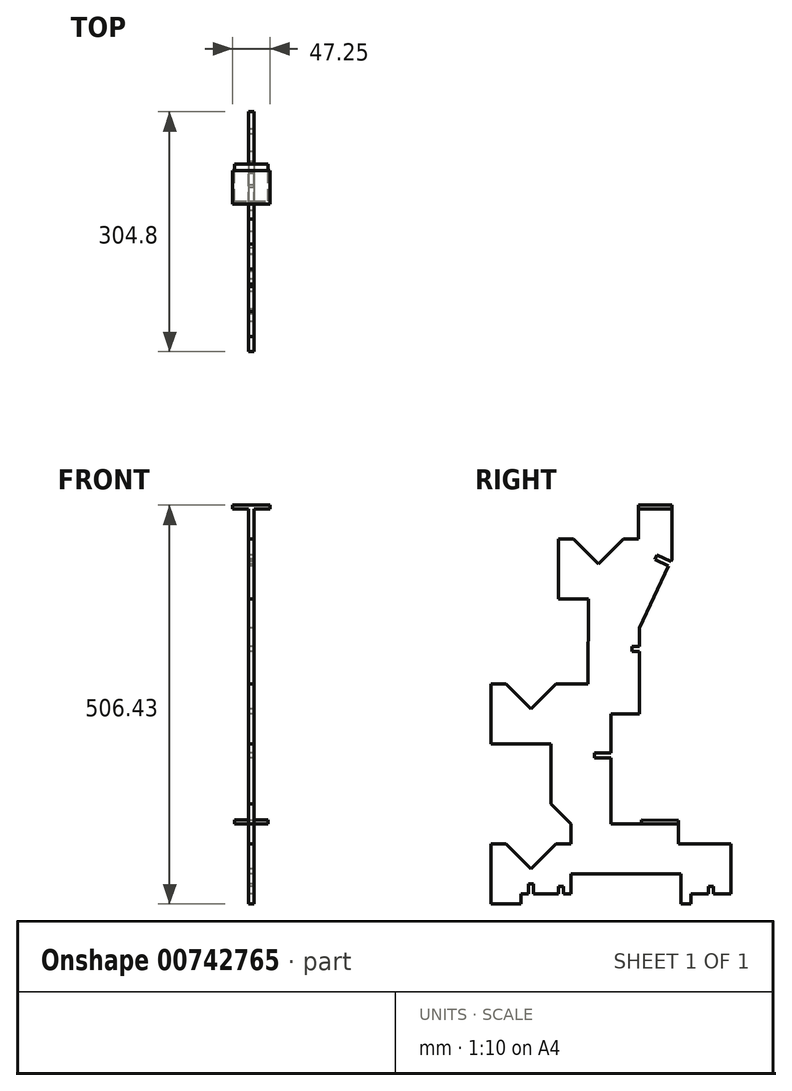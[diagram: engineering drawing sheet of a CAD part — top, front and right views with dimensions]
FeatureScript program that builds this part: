
annotation { "Feature Type Name" : "Feature", "Feature Type Description" : "" }
export const myFeature = defineFeature(function(context is Context, id is Id, definition is map)
    precondition{}
    {
        {
            var Q0;
            Q0=qCreatedBy(makeId("Right.planeOp"),FACE);
            var sketch = newSketch(context, id + "F0", { "sketchPlane" : qUnion([Q0])});
            skLineSegment(sketch, "E0", {"start": v(-497.04, 173.21) * mm, "end": v(-516.09, 173.21) * mm});
            skLineSegment(sketch, "E1", {"start": v(-516.09, 173.21) * mm, "end": v(-516.09, 97.01) * mm});
            skLineSegment(sketch, "E2", {"start": v(-516.09, 97.01) * mm, "end": v(-477.99, 97.01) * mm});
            skLineSegment(sketch, "E3", {"start": v(-477.99, 97.01) * mm, "end": v(-477.99, 109.71) * mm});
            skLineSegment(sketch, "E4", {"start": v(-477.99, 109.71) * mm, "end": v(-468.46, 109.71) * mm});
            skLineSegment(sketch, "E5", {"start": v(-414.49, 109.71) * mm, "end": v(-414.49, 135.11) * mm});
            skLineSegment(sketch, "E6", {"start": v(-433.54, 173.21) * mm, "end": v(-465.29, 141.46) * mm});
            skLineSegment(sketch, "E7", {"start": v(-465.29, 141.46) * mm, "end": v(-497.04, 173.21) * mm});
            skLineSegment(sketch, "E8", {"start": v(-414.49, 135.11) * mm, "end": v(-274.79, 135.11) * mm});
            skLineSegment(sketch, "E9", {"start": v(-277.55, 173.21) * mm, "end": v(-277.55, 198.5) * mm});
            skLineSegment(sketch, "E10", {"start": v(-277.55, 198.5) * mm, "end": v(-363.69, 198.7) * mm});
            skLineSegment(sketch, "E11.top", {"start": v(-277.55, 173.21) * mm, "end": v(-211.29, 173.21) * mm});
            skLineSegment(sketch, "E11.right", {"start": v(-211.29, 109.71) * mm, "end": v(-211.29, 173.21) * mm});
            skLineSegment(sketch, "E12.bottom", {"start": v(-274.79, 97.01) * mm, "end": v(-262.09, 97.01) * mm});
            skLineSegment(sketch, "E12.left", {"start": v(-274.79, 97.01) * mm, "end": v(-274.79, 135.11) * mm});
            skLineSegment(sketch, "E13.top", {"start": v(-211.29, 109.71) * mm, "end": v(-233.51, 109.71) * mm});
            skLineSegment(sketch, "E13.right", {"start": v(-262.09, 97.01) * mm, "end": v(-262.09, 109.71) * mm});
            skLineSegment(sketch, "E14", {"start": v(-497.04, 376.41) * mm, "end": v(-516.09, 376.41) * mm});
            skLineSegment(sketch, "E15", {"start": v(-516.09, 376.41) * mm, "end": v(-516.09, 300.21) * mm});
            skLineSegment(sketch, "E16", {"start": v(-516.09, 300.21) * mm, "end": v(-439.89, 300.21) * mm});
            skLineSegment(sketch, "E17", {"start": v(-414.49, 173.21) * mm, "end": v(-414.49, 198.61) * mm});
            skLineSegment(sketch, "E18", {"start": v(-392.73, 376.41) * mm, "end": v(-433.54, 376.41) * mm});
            skLineSegment(sketch, "E19", {"start": v(-433.54, 376.41) * mm, "end": v(-465.29, 344.66) * mm});
            skLineSegment(sketch, "E20", {"start": v(-465.29, 344.66) * mm, "end": v(-497.04, 376.41) * mm});
            skLineSegment(sketch, "E21.trimOffspring", {"start": v(-363.69, 338.31) * mm, "end": v(-327.04, 338.31) * mm});
            skLineSegment(sketch, "E22.trimOffspring", {"start": v(-414.49, 173.21) * mm, "end": v(-433.54, 173.21) * mm});
            skPoint(sketch, "E23", {"position": v(-379.41, 528.82) * mm});
            skLineSegment(sketch, "E24", {"start": v(-411.17, 560.57) * mm, "end": v(-430.22, 560.57) * mm});
            skLineSegment(sketch, "E25", {"start": v(-430.22, 560.57) * mm, "end": v(-430.22, 484.37) * mm});
            skLineSegment(sketch, "E26", {"start": v(-430.22, 484.37) * mm, "end": v(-392.12, 484.37) * mm});
            skLineSegment(sketch, "E27", {"start": v(-347.67, 560.57) * mm, "end": v(-379.43, 528.84) * mm});
            skLineSegment(sketch, "E28", {"start": v(-379.43, 528.84) * mm, "end": v(-411.17, 560.57) * mm});
            skLineSegment(sketch, "E29.trimOffspring", {"start": v(-328.62, 560.57) * mm, "end": v(-347.67, 560.57) * mm});
            skLineSegment(sketch, "E30.bottom", {"start": v(-328.62, 598.67) * mm, "end": v(-286.03, 598.67) * mm});
            skLineSegment(sketch, "E30.right", {"start": v(-286.03, 598.67) * mm, "end": v(-286.03, 535.17) * mm});
            skLineSegment(sketch, "E31.0", {"start": v(-328.62, 560.57) * mm, "end": v(-328.62, 598.67) * mm});
            skLineSegment(sketch, "E32", {"start": v(-290.14, 526.35) * mm, "end": v(-327.04, 447.21) * mm});
            skLineSegment(sketch, "E33.0", {"start": v(-304.72, 540.16) * mm, "end": v(-307.4, 534.4) * mm});
            skLineSegment(sketch, "E34", {"start": v(-290.14, 526.35) * mm, "end": v(-307.4, 534.4) * mm});
            skLineSegment(sketch, "E35.0", {"start": v(-287.46, 532.1) * mm, "end": v(-304.72, 540.16) * mm});
            skLineSegment(sketch, "E36.trimOffspring", {"start": v(-286.03, 535.17) * mm, "end": v(-287.46, 532.1) * mm});
            skLineSegment(sketch, "E37", {"start": v(-392.12, 484.37) * mm, "end": v(-392.73, 376.41) * mm});
            skLineSegment(sketch, "E38", {"start": v(-327.04, 447.21) * mm, "end": v(-327.04, 424.11) * mm});
            skLineSegment(sketch, "E39.0", {"start": v(-379.42, 571.49) * mm, "end": v(-400.76, 550.17) * mm, "construction": true});
            skLineSegment(sketch, "E40.0", {"start": v(-358.09, 550.15) * mm, "end": v(-379.42, 571.49) * mm, "construction": true});
            skLineSegment(sketch, "E41", {"start": v(-379.42, 571.49) * mm, "end": v(-288.8, 529.23) * mm, "construction": true});
            skLineSegment(sketch, "E42.0", {"start": v(-443.96, 366) * mm, "end": v(-465.29, 387.32) * mm, "construction": true});
            skLineSegment(sketch, "E43.0", {"start": v(-465.29, 387.32) * mm, "end": v(-486.62, 366) * mm, "construction": true});
            skLineSegment(sketch, "E44.0", {"start": v(-465.29, 184.12) * mm, "end": v(-486.62, 162.8) * mm, "construction": true});
            skLineSegment(sketch, "E45.0", {"start": v(-443.96, 162.8) * mm, "end": v(-465.29, 184.12) * mm, "construction": true});
            skLineSegment(sketch, "E46", {"start": v(-465.29, 184.12) * mm, "end": v(-414.49, 184.12) * mm, "construction": true});
            skLineSegment(sketch, "E47", {"start": v(-465.29, 387.32) * mm, "end": v(-392.67, 386.9) * mm, "construction": true});
            skLineSegment(sketch, "E48.0", {"start": v(-384.33, 282.07) * mm, "end": v(-363.69, 282.07) * mm});
            skLineSegment(sketch, "E49.0", {"start": v(-384.33, 288.42) * mm, "end": v(-363.69, 288.42) * mm});
            skLineSegment(sketch, "E50.0", {"start": v(-439.89, 224.01) * mm, "end": v(-439.89, 300.21) * mm});
            skLineSegment(sketch, "E51", {"start": v(-414.49, 198.61) * mm, "end": v(-439.89, 224.01) * mm});
            skLineSegment(sketch, "E52.0", {"start": v(-363.69, 198.7) * mm, "end": v(-363.69, 282.07) * mm});
            skLineSegment(sketch, "E53.trimOffspring", {"start": v(-363.69, 288.42) * mm, "end": v(-363.69, 338.31) * mm});
            skLineSegment(sketch, "E54.0", {"start": v(-384.33, 282.07) * mm, "end": v(-384.33, 288.42) * mm});
            skLineSegment(sketch, "E55.0", {"start": v(-468.46, 122.41) * mm, "end": v(-468.46, 109.71) * mm});
            skLineSegment(sketch, "E56.0", {"start": v(-462.11, 122.41) * mm, "end": v(-462.11, 109.71) * mm});
            skLineSegment(sketch, "E57.0", {"start": v(-468.46, 122.41) * mm, "end": v(-462.11, 122.41) * mm});
            skLineSegment(sketch, "E58.trimOffspring", {"start": v(-462.11, 109.71) * mm, "end": v(-430.36, 109.71) * mm});
            skLineSegment(sketch, "E59.0", {"start": v(-336.97, 417.82) * mm, "end": v(-327.04, 417.76) * mm});
            skLineSegment(sketch, "E60.0", {"start": v(-336.93, 424.17) * mm, "end": v(-327.04, 424.11) * mm});
            skLineSegment(sketch, "E61.0", {"start": v(-336.93, 424.17) * mm, "end": v(-336.97, 417.82) * mm});
            skLineSegment(sketch, "E62.trimOffspring", {"start": v(-327.04, 417.76) * mm, "end": v(-327.04, 338.31) * mm});
            skLineSegment(sketch, "E63.top", {"start": v(-239.86, 119.24) * mm, "end": v(-233.51, 119.24) * mm});
            skLineSegment(sketch, "E63.left", {"start": v(-239.86, 109.71) * mm, "end": v(-239.86, 119.24) * mm});
            skLineSegment(sketch, "E63.right", {"start": v(-233.51, 109.71) * mm, "end": v(-233.51, 119.24) * mm});
            skLineSegment(sketch, "E64.trimOffspring", {"start": v(-239.86, 109.71) * mm, "end": v(-262.09, 109.71) * mm});
            skLineSegment(sketch, "E65.bottom", {"start": v(-424.01, 119.24) * mm, "end": v(-430.36, 119.24) * mm});
            skLineSegment(sketch, "E65.left", {"start": v(-424.01, 119.24) * mm, "end": v(-424.01, 109.71) * mm});
            skLineSegment(sketch, "E65.right", {"start": v(-430.36, 119.24) * mm, "end": v(-430.36, 109.71) * mm});
            skLineSegment(sketch, "E66.trimOffspring", {"start": v(-424.01, 109.71) * mm, "end": v(-414.49, 109.71) * mm});
            skSolve(sketch);
        }
        {
            var Q0;
            Q0=qSketchRegion(id+"F0",true);
            extrude(context, id + "F1", {"entities" : qUnion([Q0]), "depth" : 6.35 * mm, "offsetDistance" : 25.4 * mm});
        }
        {
            var Q0;
            Q0=makeQuery(id+"F1.opExtrude","SWEPT_FACE",FACE,{"disambiguationData":[OSD([sQuery(id+"F0.wireOp",EDGE,"E30.bottom")])]});
            var sketch = newSketch(context, id + "F2", { "sketchPlane" : qUnion([Q0])});
            skLineSegment(sketch, "E67.bottom", {"start": v(-20.45, -328.62) * mm, "end": v(26.8, -328.62) * mm});
            skLineSegment(sketch, "E67.top", {"start": v(-20.45, -286.03) * mm, "end": v(26.8, -286.03) * mm});
            skLineSegment(sketch, "E67.left", {"start": v(-20.45, -328.62) * mm, "end": v(-20.45, -286.03) * mm});
            skLineSegment(sketch, "E67.right", {"start": v(26.8, -328.62) * mm, "end": v(26.8, -286.03) * mm});
            skSolve(sketch);
        }
        {
            var Q0;
            Q0=qSketchRegion(id+"F2",true);
            extrude(context, id + "F3", {"entities" : qUnion([Q0]), "operationType" : NewBodyOperationType.ADD, "depth" : 4.76 * mm, "offsetDistance" : 25.4 * mm});
        }
        {
            var Q0;
            Q0=makeQuery(id+"F1.opExtrude","SWEPT_FACE",FACE,{"disambiguationData":[OSD([sQuery(id+"F0.wireOp",EDGE,"E10")])]});
            var sketch = newSketch(context, id + "F4", { "sketchPlane" : qUnion([Q0])});
            skLineSegment(sketch, "E68.bottom", {"start": v(-18.12, -325.23) * mm, "end": v(24.47, -325.23) * mm});
            skLineSegment(sketch, "E68.top", {"start": v(-18.12, -277.98) * mm, "end": v(24.47, -277.98) * mm});
            skLineSegment(sketch, "E68.left", {"start": v(-18.12, -325.23) * mm, "end": v(-18.12, -277.98) * mm});
            skLineSegment(sketch, "E68.right", {"start": v(24.47, -325.23) * mm, "end": v(24.47, -277.98) * mm});
            skSolve(sketch);
        }
        {
            var Q0;
            Q0=qSketchRegion(id+"F4",true);
            extrude(context, id + "F5", {"entities" : qUnion([Q0]), "operationType" : NewBodyOperationType.ADD, "depth" : 4.76 * mm, "offsetDistance" : 25.4 * mm});
        }
    });
